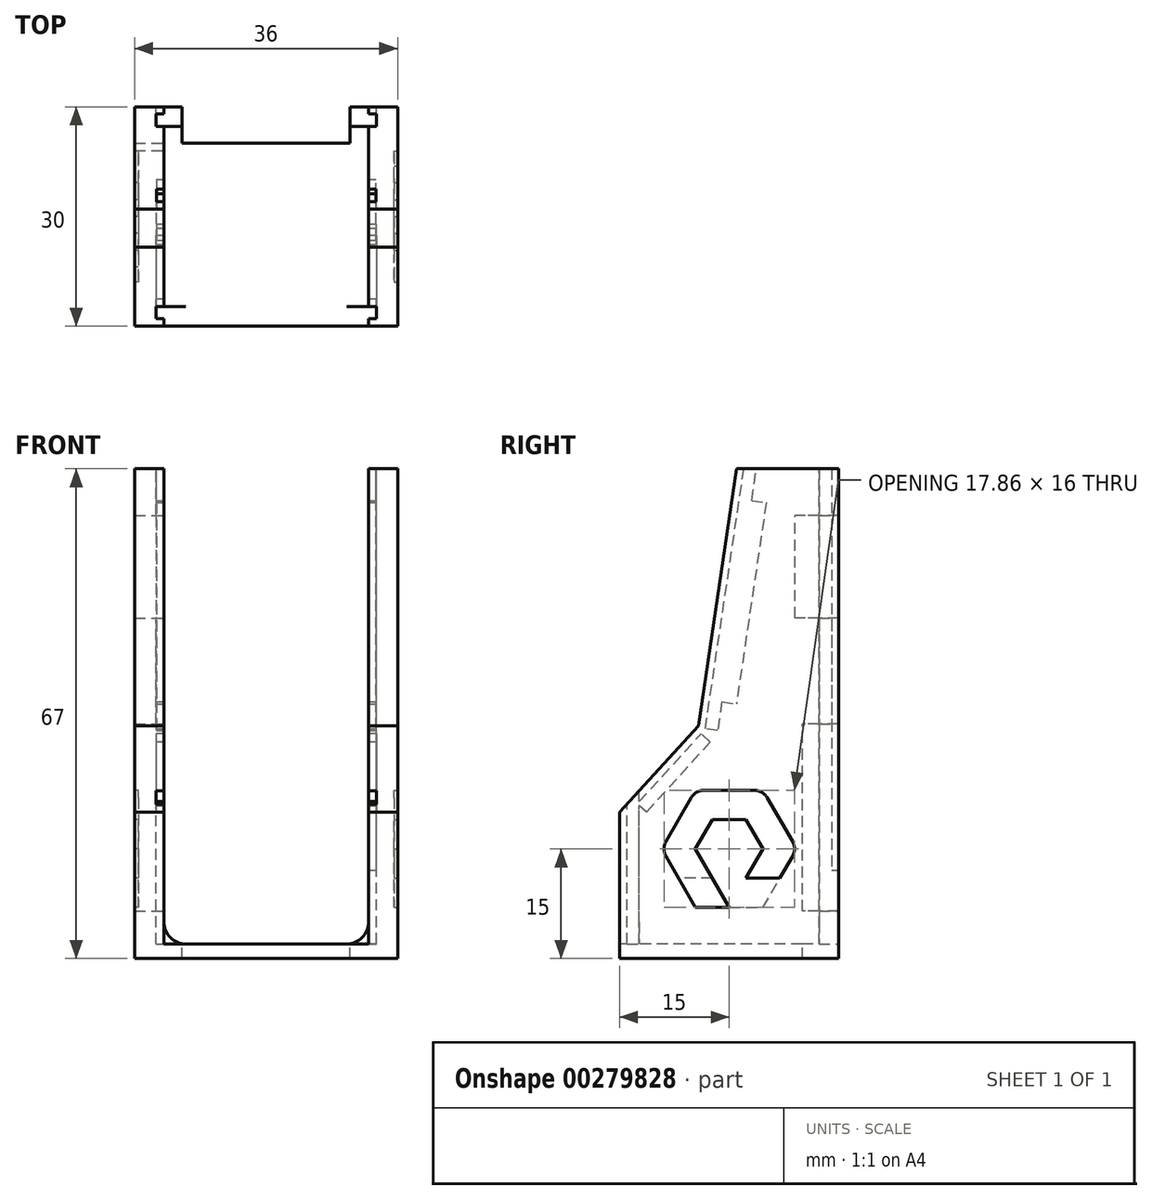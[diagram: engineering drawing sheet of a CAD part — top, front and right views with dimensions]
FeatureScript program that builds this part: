
annotation { "Feature Type Name" : "Feature", "Feature Type Description" : "" }
export const myFeature = defineFeature(function(context is Context, id is Id, definition is map)
    precondition{}
    {
        {
            var Q0;
            Q0=qCreatedBy(makeId("Right.planeOp"),FACE);
            var sketch = newSketch(context, id + "F0", { "sketchPlane" : qUnion([Q0])});
            skLineSegment(sketch, "E0", {"start": v(0, 0) * mm, "end": v(0, 67) * mm});
            skLineSegment(sketch, "E1", {"start": v(-14, 67) * mm, "end": v(-19.22, 31.83) * mm});
            skLineSegment(sketch, "E2", {"start": v(-19.22, 31.83) * mm, "end": v(-30, 20) * mm});
            skLineSegment(sketch, "E3", {"start": v(-30, 20) * mm, "end": v(-30, 0) * mm});
            skLineSegment(sketch, "E4", {"start": v(-30, 0) * mm, "end": v(0, 0) * mm});
            skLineSegment(sketch, "E5", {"start": v(0, 67) * mm, "end": v(-14, 67) * mm});
            skSolve(sketch);
        }
        {
            var Q0;
            Q0 = qSketchRegion(id + "F0", true);
            extrude(context, id + "F1", {"entities" : qUnion([Q0]), "endBound" : BoundingType.SYMMETRIC, "depth" : 36 * mm});
        }
        {
            var Q0;
            Q0=qCreatedBy(makeId("Right.planeOp"),FACE);
            var sketch = newSketch(context, id + "F2", { "sketchPlane" : qUnion([Q0])});
            skLineSegment(sketch, "E6.bottom", {"start": v(0, 2) * mm, "end": v(-30, 2) * mm});
            skLineSegment(sketch, "E6.top", {"start": v(0, 82) * mm, "end": v(-30, 82) * mm});
            skLineSegment(sketch, "E6.left", {"start": v(0, 2) * mm, "end": v(0, 82) * mm});
            skLineSegment(sketch, "E6.right", {"start": v(-30, 2) * mm, "end": v(-30, 82) * mm});
            skSolve(sketch);
        }
        {
            var Q0;
            Q0 = qSketchRegion(id + "F2", true);
            extrude(context, id + "F3", {"entities" : qUnion([Q0]), "operationType" : NewBodyOperationType.REMOVE, "endBound" : BoundingType.SYMMETRIC, "oppositeDirection" : true, "depth" : 28 * mm});
        }
        {
            var Q0;
            Q0=qCreatedBy(makeId("Right.planeOp"),FACE);
            var sketch = newSketch(context, id + "F4", { "sketchPlane" : qUnion([Q0])});
            skLineSegment(sketch, "E7.bottom", {"start": v(0, 6.5) * mm, "end": v(-5, 6.5) * mm});
            skLineSegment(sketch, "E7.top", {"start": v(0, 32.1) * mm, "end": v(-5, 32.1) * mm});
            skLineSegment(sketch, "E7.left", {"start": v(0, 6.5) * mm, "end": v(0, 32.1) * mm});
            skLineSegment(sketch, "E7.right", {"start": v(-5, 6.5) * mm, "end": v(-5, 32.1) * mm});
            skLineSegment(sketch, "E8.bottom", {"start": v(0, 46.6) * mm, "end": v(-6, 46.6) * mm});
            skLineSegment(sketch, "E8.top", {"start": v(0, 60.6) * mm, "end": v(-6, 60.6) * mm});
            skLineSegment(sketch, "E8.left", {"start": v(0, 46.6) * mm, "end": v(0, 60.6) * mm});
            skLineSegment(sketch, "E8.right", {"start": v(-6, 46.6) * mm, "end": v(-6, 60.6) * mm});
            skSolve(sketch);
        }
        {
            var Q0;
            Q0 = qSketchRegion(id + "F4", true);
            extrude(context, id + "F5", {"entities" : qUnion([Q0]), "operationType" : NewBodyOperationType.REMOVE, "oppositeDirection" : true, "depth" : 25 * mm});
        }
        {
            var Q0;
            Q0=qCreatedBy(makeId("Right.planeOp"),FACE);
            var sketch = newSketch(context, id + "F6", { "sketchPlane" : qUnion([Q0])});
            skLineSegment(sketch, "E9.bottom", {"start": v(0, 0) * mm, "end": v(-5, 0) * mm});
            skLineSegment(sketch, "E9.top", {"start": v(0, 5) * mm, "end": v(-5, 5) * mm});
            skLineSegment(sketch, "E9.left", {"start": v(0, 0) * mm, "end": v(0, 5) * mm});
            skLineSegment(sketch, "E9.right", {"start": v(-5, 0) * mm, "end": v(-5, 5) * mm});
            skSolve(sketch);
        }
        {
            var Q0;
            Q0 = qSketchRegion(id + "F6", true);
            extrude(context, id + "F7", {"entities" : qUnion([Q0]), "operationType" : NewBodyOperationType.REMOVE, "endBound" : BoundingType.SYMMETRIC, "oppositeDirection" : true, "depth" : 23 * mm});
        }
        {
            var Q0;
            Q0=qCreatedBy(makeId("Right.planeOp"),FACE);
            var sketch = newSketch(context, id + "F8", { "sketchPlane" : qUnion([Q0])});
            skLineSegment(sketch, "E10.bottom", {"start": v(-2.7, 2) * mm, "end": v(-1, 2) * mm});
            skLineSegment(sketch, "E10.top", {"start": v(-2.7, 67) * mm, "end": v(-1, 67) * mm});
            skLineSegment(sketch, "E10.left", {"start": v(-2.7, 2) * mm, "end": v(-2.7, 67) * mm});
            skLineSegment(sketch, "E10.right", {"start": v(-1, 2) * mm, "end": v(-1, 67) * mm});
            skLineSegment(sketch, "E11.bottom", {"start": v(-1, 2) * mm, "end": v(9, 2) * mm});
            skLineSegment(sketch, "E11.top", {"start": v(-1, 12) * mm, "end": v(9, 12) * mm});
            skLineSegment(sketch, "E11.left", {"start": v(-1, 2) * mm, "end": v(-1, 12) * mm});
            skLineSegment(sketch, "E11.right", {"start": v(9, 2) * mm, "end": v(9, 12) * mm});
            skSolve(sketch);
        }
        {
            var Q0;
            Q0 = qSketchRegion(id + "F8", true);
            extrude(context, id + "F9", {"entities" : qUnion([Q0]), "operationType" : NewBodyOperationType.REMOVE, "endBound" : BoundingType.SYMMETRIC, "depth" : 30.2 * mm});
        }
        {
            var Q0;
            Q0=qCreatedBy(makeId("Right.planeOp"),FACE);
            var sketch = newSketch(context, id + "F10", { "sketchPlane" : qUnion([Q0])});
            skLineSegment(sketch, "E12.bottom", {"start": v(-29, 2) * mm, "end": v(-27.3, 2) * mm});
            skLineSegment(sketch, "E12.top", {"start": v(-29, 19.78) * mm, "end": v(-27.3, 19.78) * mm});
            skLineSegment(sketch, "E12.left", {"start": v(-29, 2) * mm, "end": v(-29, 19.78) * mm});
            skLineSegment(sketch, "E12.right", {"start": v(-27.3, 2) * mm, "end": v(-27.3, 19.78) * mm});
            skLineSegment(sketch, "E13.top", {"start": v(-29, 29.78) * mm, "end": v(-27.3, 29.78) * mm});
            skLineSegment(sketch, "E13.left", {"start": v(-29, 19.78) * mm, "end": v(-29, 29.78) * mm});
            skLineSegment(sketch, "E13.right", {"start": v(-27.3, 19.78) * mm, "end": v(-27.3, 29.78) * mm});
            skSolve(sketch);
        }
        {
            var Q0;
            Q0 = qSketchRegion(id + "F10", true);
            extrude(context, id + "F11", {"entities" : qUnion([Q0]), "operationType" : NewBodyOperationType.REMOVE, "endBound" : BoundingType.SYMMETRIC, "oppositeDirection" : true, "depth" : 30.2 * mm});
        }
        {
            var Q0;
            Q0=qCreatedBy(makeId("Right.planeOp"),FACE);
            var sketch = newSketch(context, id + "F12", { "sketchPlane" : qUnion([Q0])});
            skLineSegment(sketch, "E14.bottom", {"start": v(-18.85, 30.75) * mm, "end": v(-27.58, 21.17) * mm});
            skLineSegment(sketch, "E14.top", {"start": v(-17.6, 29.6) * mm, "end": v(-26.32, 20.03) * mm});
            skLineSegment(sketch, "E14.left", {"start": v(-18.85, 30.75) * mm, "end": v(-17.6, 29.6) * mm});
            skLineSegment(sketch, "E14.right", {"start": v(-27.58, 21.17) * mm, "end": v(-26.32, 20.03) * mm});
            skPoint(sketch, "E14.middle", {"position": v(-22.59, 25.39) * mm});
            skSolve(sketch);
        }
        {
            var Q0;
            Q0 = qSketchRegion(id + "F12", true);
            extrude(context, id + "F13", {"entities" : qUnion([Q0]), "operationType" : NewBodyOperationType.REMOVE, "endBound" : BoundingType.SYMMETRIC, "depth" : 30.2 * mm});
        }
        {
            var Q0;
            Q0=qCreatedBy(makeId("Right.planeOp"),FACE);
            var sketch = newSketch(context, id + "F14", { "sketchPlane" : qUnion([Q0])});
            skLineSegment(sketch, "E15.bottom", {"start": v(-11.33, 66.6) * mm, "end": v(-16.59, 31.18) * mm});
            skLineSegment(sketch, "E15.top", {"start": v(-13.01, 66.85) * mm, "end": v(-18.27, 31.43) * mm});
            skLineSegment(sketch, "E15.left", {"start": v(-11.33, 66.6) * mm, "end": v(-13.01, 66.85) * mm});
            skLineSegment(sketch, "E15.right", {"start": v(-16.59, 31.18) * mm, "end": v(-18.27, 31.43) * mm});
            skPoint(sketch, "E15.middle", {"position": v(-14.8, 49.02) * mm});
            skLineSegment(sketch, "E16.bottom", {"start": v(-13.01, 66.85) * mm, "end": v(-11.33, 66.6) * mm});
            skLineSegment(sketch, "E16.top", {"start": v(-11.54, 76.74) * mm, "end": v(-9.86, 76.5) * mm});
            skLineSegment(sketch, "E16.left", {"start": v(-13.01, 66.85) * mm, "end": v(-11.54, 76.74) * mm});
            skLineSegment(sketch, "E16.right", {"start": v(-11.33, 66.6) * mm, "end": v(-9.86, 76.5) * mm});
            skLineSegment(sketch, "E17.bottom", {"start": v(-11.92, 62.65) * mm, "end": v(-16, 35.13) * mm});
            skLineSegment(sketch, "E17.top", {"start": v(-9.94, 62.35) * mm, "end": v(-14.02, 34.84) * mm});
            skLineSegment(sketch, "E17.left", {"start": v(-11.92, 62.65) * mm, "end": v(-9.94, 62.35) * mm});
            skLineSegment(sketch, "E17.right", {"start": v(-16, 35.13) * mm, "end": v(-14.02, 34.84) * mm});
            skPoint(sketch, "E17.middle", {"position": v(-12.97, 48.74) * mm});
            skSolve(sketch);
        }
        {
            var Q0;
            Q0 = qSketchRegion(id + "F14", true);
            extrude(context, id + "F15", {"entities" : qUnion([Q0]), "operationType" : NewBodyOperationType.REMOVE, "endBound" : BoundingType.SYMMETRIC, "oppositeDirection" : true, "depth" : 30 * mm});
        }
        {
            var Q0;
            Q0=makeQuery(id+"F1.opExtrude","CAP_FACE",FACE,{"disambiguationData":[OSD([sQuery(id+"F0.wireOp",EDGE,"E0"),sQuery(id+"F0.wireOp",EDGE,"E1"),sQuery(id+"F0.wireOp",EDGE,"E2"),sQuery(id+"F0.wireOp",EDGE,"E3"),sQuery(id+"F0.wireOp",EDGE,"E4"),sQuery(id+"F0.wireOp",EDGE,"E5")])],"isStart":false});
            var sketch = newSketch(context, id + "F16", { "sketchPlane" : qUnion([Q0])});
            skCircle(sketch, "E18.cCircle", {"center": v(-15, 15) * mm, "radius": 8 * mm, "construction": true});
            skLineSegment(sketch, "E18.0", {"start": v(-10.38, 7) * mm, "end": v(-19.62, 7) * mm});
            skLineSegment(sketch, "E18.1", {"start": v(-19.62, 7) * mm, "end": v(-23.66, 14) * mm});
            skLineSegment(sketch, "E18.2", {"start": v(-23.66, 16) * mm, "end": v(-20.2, 22) * mm});
            skLineSegment(sketch, "E18.3", {"start": v(-18.46, 23) * mm, "end": v(-11.54, 23) * mm});
            skLineSegment(sketch, "E18.4", {"start": v(-9.8, 22) * mm, "end": v(-6.34, 16) * mm});
            skLineSegment(sketch, "E18.5", {"start": v(-6.34, 14) * mm, "end": v(-10.38, 7) * mm});
            skPoint(sketch, "E18.0.midPoint", {"position": v(-15, 7) * mm});
            skLineSegment(sketch, "E19.0", {"start": v(-19.62, 15) * mm, "end": v(-17.3, 19) * mm});
            skLineSegment(sketch, "E19.1", {"start": v(-12.7, 19) * mm, "end": v(-10.38, 15) * mm});
            skLineSegment(sketch, "E19.2", {"start": v(-10.38, 15) * mm, "end": v(-12.7, 11) * mm});
            skLineSegment(sketch, "E19.3", {"start": v(-17.3, 19) * mm, "end": v(-12.7, 19) * mm});
            skLineSegment(sketch, "E19.4", {"start": v(-12.7, 11) * mm, "end": v(-17.3, 11) * mm});
            skLineSegment(sketch, "E19.5", {"start": v(-17.3, 11) * mm, "end": v(-19.62, 15) * mm});
            skLineSegment(sketch, "E20", {"start": v(-12.7, 11) * mm, "end": v(-8.07, 11) * mm});
            skLineSegment(sketch, "E21", {"start": v(-17.3, 11) * mm, "end": v(-15, 7) * mm});
            skPoint(sketch, "E22.visualSharp", {"position": v(-19.62, 23) * mm});
            skArc(sketch, "E22.filletArc", {"start": v(-18.46, 23) * mm, "mid": v(-19.46, 22.73) * mm, "end": v(-20.2, 22) * mm});
            skPoint(sketch, "E23.visualSharp", {"position": v(-10.38, 23) * mm});
            skArc(sketch, "E23.filletArc", {"start": v(-9.8, 22) * mm, "mid": v(-10.54, 22.73) * mm, "end": v(-11.54, 23) * mm});
            skPoint(sketch, "E24.visualSharp", {"position": v(-24.24, 15) * mm});
            skArc(sketch, "E24.filletArc", {"start": v(-23.66, 16) * mm, "mid": v(-23.93, 15) * mm, "end": v(-23.66, 14) * mm});
            skPoint(sketch, "E25.visualSharp", {"position": v(-5.76, 15) * mm});
            skArc(sketch, "E25.filletArc", {"start": v(-6.34, 14) * mm, "mid": v(-6.07, 15) * mm, "end": v(-6.34, 16) * mm});
            skSolve(sketch);
        }
        {
            var Q0;
            {var subQ3=sQuery(id+"F16.wireOp",EDGE,"E18.1");Q0=makeQuery(id+"F16.imprint","IMPRINT",FACE,{"disambiguationData":[TD([[makeQuery(id+"F16.imprint","IMPRINT",EDGE,{"derivedFrom":subQ3}),-1.0]])]});}
            extrude(context, id + "F17", {"entities" : qUnion([Q0]), "operationType" : NewBodyOperationType.REMOVE, "oppositeDirection" : true, "depth" : .5 * mm});
        }
        {
            var Q0;
            Q0=makeQuery(id+"F1.opExtrude","CAP_FACE",FACE,{"disambiguationData":[OSD([sQuery(id+"F0.wireOp",EDGE,"E0"),sQuery(id+"F0.wireOp",EDGE,"E1"),sQuery(id+"F0.wireOp",EDGE,"E2"),sQuery(id+"F0.wireOp",EDGE,"E3"),sQuery(id+"F0.wireOp",EDGE,"E4"),sQuery(id+"F0.wireOp",EDGE,"E5")])],"isStart":true});
            var sketch = newSketch(context, id + "F18", { "sketchPlane" : qUnion([Q0])});
            skCircle(sketch, "E26.cCircle", {"center": v(15, 15) * mm, "radius": 8 * mm, "construction": true});
            skLineSegment(sketch, "E26.0", {"start": v(11.54, 23) * mm, "end": v(18.46, 23) * mm});
            skLineSegment(sketch, "E26.1", {"start": v(20.2, 22) * mm, "end": v(23.66, 16) * mm});
            skLineSegment(sketch, "E26.2", {"start": v(23.66, 14) * mm, "end": v(19.62, 7) * mm});
            skLineSegment(sketch, "E26.3", {"start": v(19.62, 7) * mm, "end": v(10.38, 7) * mm});
            skLineSegment(sketch, "E26.4", {"start": v(10.38, 7) * mm, "end": v(6.34, 14) * mm});
            skLineSegment(sketch, "E26.5", {"start": v(6.34, 16) * mm, "end": v(9.8, 22) * mm});
            skPoint(sketch, "E26.0.midPoint", {"position": v(15, 23) * mm});
            skLineSegment(sketch, "E27.0", {"start": v(17.3, 11) * mm, "end": v(12.7, 11) * mm});
            skLineSegment(sketch, "E27.1", {"start": v(10.38, 15) * mm, "end": v(12.7, 19) * mm});
            skLineSegment(sketch, "E27.2", {"start": v(12.7, 19) * mm, "end": v(17.3, 19) * mm});
            skLineSegment(sketch, "E27.3", {"start": v(12.7, 11) * mm, "end": v(10.38, 15) * mm});
            skLineSegment(sketch, "E27.4", {"start": v(17.3, 19) * mm, "end": v(19.62, 15) * mm});
            skLineSegment(sketch, "E27.5", {"start": v(19.62, 15) * mm, "end": v(17.3, 11) * mm});
            skLineSegment(sketch, "E28", {"start": v(12.7, 11) * mm, "end": v(15, 7) * mm});
            skLineSegment(sketch, "E29", {"start": v(17.3, 11) * mm, "end": v(21.93, 11) * mm});
            skPoint(sketch, "E30.visualSharp", {"position": v(10.38, 23) * mm});
            skArc(sketch, "E30.filletArc", {"start": v(11.54, 23) * mm, "mid": v(10.54, 22.73) * mm, "end": v(9.8, 22) * mm});
            skPoint(sketch, "E31.visualSharp", {"position": v(19.62, 23) * mm});
            skArc(sketch, "E31.filletArc", {"start": v(20.2, 22) * mm, "mid": v(19.46, 22.73) * mm, "end": v(18.46, 23) * mm});
            skPoint(sketch, "E32.visualSharp", {"position": v(24.24, 15) * mm});
            skArc(sketch, "E32.filletArc", {"start": v(23.66, 14) * mm, "mid": v(23.93, 15) * mm, "end": v(23.66, 16) * mm});
            skPoint(sketch, "E33.visualSharp", {"position": v(5.76, 15) * mm});
            skArc(sketch, "E33.filletArc", {"start": v(6.34, 16) * mm, "mid": v(6.07, 15) * mm, "end": v(6.34, 14) * mm});
            skSolve(sketch);
        }
        {
            var Q0;
            Q0=makeQuery(id+"F18.imprint","IMPRINT",FACE,{"disambiguationData":[TD([[makeQuery(id+"F18.imprint","IMPRINT",EDGE,{"derivedFrom":sQuery(id+"F18.wireOp",EDGE,"E26.0")}),-1.0]])]});
            extrude(context, id + "F19", {"entities" : qUnion([Q0]), "operationType" : NewBodyOperationType.REMOVE, "oppositeDirection" : true, "depth" : .5 * mm});
        }
        {
            var Q0;
            {var subQ2=sQuery(id+"F2.wireOp",EDGE,"E6.bottom");Q0=makeQuery(id+"F11.boolean.opBoolean","SPLIT",EDGE,{"disambiguationData":[TD([makeQuery(id+"F11.opExtrude","SWEPT_FACE",FACE,{"disambiguationData":[OSD([sQuery(id+"F10.wireOp",EDGE,"E12.right"),sQuery(id+"F10.wireOp",EDGE,"E13.right")])]})])],"derivedFrom":makeQuery(id+"F3.boolean.opBoolean","COPY",EDGE,{"derivedFrom":makeQuery(id+"F3.opExtrude","CAP_EDGE",EDGE,{"disambiguationData":[OSD([subQ2])],"isStart":false})})});}
            fillet(context, id + "F20", {"entities" : qUnion([Q0]), "radius" : 3 * mm, "tangentPropagation" : true, "allowEdgeOverflow" : false});
        }
        {
            var Q0;
            {var subQ0=sQuery(id+"F2.wireOp",EDGE,"E6.bottom");Q0=makeQuery(id+"F11.boolean.opBoolean","SPLIT",EDGE,{"disambiguationData":[TD([makeQuery(id+"F11.opExtrude","SWEPT_FACE",FACE,{"disambiguationData":[OSD([sQuery(id+"F10.wireOp",EDGE,"E12.right"),sQuery(id+"F10.wireOp",EDGE,"E13.right")])]})])],"derivedFrom":makeQuery(id+"F3.boolean.opBoolean","COPY",EDGE,{"derivedFrom":makeQuery(id+"F3.opExtrude","CAP_EDGE",EDGE,{"disambiguationData":[OSD([subQ0])],"isStart":true})})});}
            fillet(context, id + "F21", {"entities" : qUnion([Q0]), "radius" : 3 * mm, "tangentPropagation" : true, "allowEdgeOverflow" : false});
        }
    });
